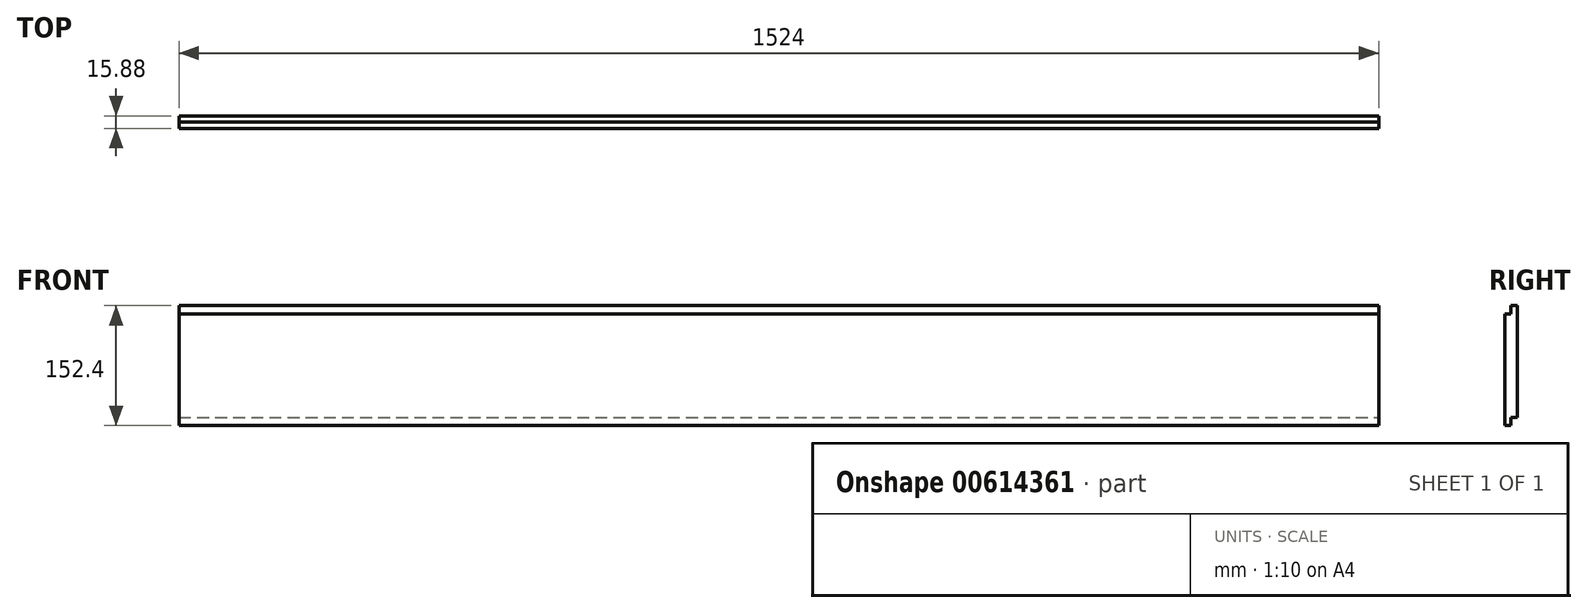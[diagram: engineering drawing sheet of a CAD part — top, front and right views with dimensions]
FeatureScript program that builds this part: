
annotation { "Feature Type Name" : "Feature", "Feature Type Description" : "" }
export const myFeature = defineFeature(function(context is Context, id is Id, definition is map)
    precondition{}
    {
        {
            var Q0;
            Q0=qCreatedBy(makeId("Front.planeOp"),FACE);
            var sketch = newSketch(context, id + "F0", { "sketchPlane" : qUnion([Q0])});
            skLineSegment(sketch, "E0", {"start": v(0, 0) * mm, "end": v(762, 0) * mm});
            skLineSegment(sketch, "E1", {"start": v(762, 0) * mm, "end": v(762, 76.2) * mm});
            skLineSegment(sketch, "E2.bottom", {"start": v(762, 76.2) * mm, "end": v(-762, 76.2) * mm});
            skLineSegment(sketch, "E2.top", {"start": v(762, -76.2) * mm, "end": v(-762, -76.2) * mm});
            skLineSegment(sketch, "E2.left", {"start": v(762, 76.2) * mm, "end": v(762, -76.2) * mm});
            skLineSegment(sketch, "E2.right", {"start": v(-762, 76.2) * mm, "end": v(-762, -76.2) * mm});
            skPoint(sketch, "E2.middle", {"position": v(0, 0) * mm});
            skSolve(sketch);
        }
        {
            var Q0;
            Q0=qSketchRegion(id+"F0",true);
            extrude(context, id + "F1", {"entities" : qUnion([Q0]), "depth" : 15.88 * mm, "offsetDistance" : 25.4 * mm});
        }
        {
            var Q0;
            Q0=makeQuery(id+"F1.opExtrude","SWEPT_FACE",FACE,{"disambiguationData":[OSD([sQuery(id+"F0.wireOp",EDGE,"E2.left")])]});
            var sketch = newSketch(context, id + "F2", { "sketchPlane" : qUnion([Q0])});
            skLineSegment(sketch, "E3", {"start": v(0, 76.2) * mm, "end": v(-7.87, 76.2) * mm});
            skLineSegment(sketch, "E4", {"start": v(-7.87, 76.2) * mm, "end": v(-7.87, 65.79) * mm});
            skLineSegment(sketch, "E5.bottom", {"start": v(-15.88, 76.2) * mm, "end": v(-7.87, 76.2) * mm});
            skLineSegment(sketch, "E5.top", {"start": v(-15.88, 65.79) * mm, "end": v(-7.87, 65.79) * mm});
            skLineSegment(sketch, "E5.left", {"start": v(-15.88, 76.2) * mm, "end": v(-15.88, 65.79) * mm});
            skLineSegment(sketch, "E6", {"start": v(-15.88, -76.2) * mm, "end": v(-8, -76.2) * mm});
            skLineSegment(sketch, "E7", {"start": v(-8, -76.2) * mm, "end": v(-8, -65.79) * mm});
            skLineSegment(sketch, "E8.bottom", {"start": v(0, -76.2) * mm, "end": v(-8, -76.2) * mm});
            skLineSegment(sketch, "E8.top", {"start": v(0, -65.79) * mm, "end": v(-8, -65.79) * mm});
            skLineSegment(sketch, "E8.left", {"start": v(0, -76.2) * mm, "end": v(0, -65.79) * mm});
            skSolve(sketch);
        }
        {
            var Q0;
            Q0=makeQuery(id+"F2.imprint","IMPRINT",FACE,{"disambiguationData":[TD([[makeQuery(id+"F2.imprint","IMPRINT",EDGE,{"derivedFrom":sQuery(id+"F2.wireOp",EDGE,"E8.bottom")}),1.0]])]});
            var Q1;
            Q1=makeQuery(id+"F2.imprint","IMPRINT",FACE,{"disambiguationData":[TD([[makeQuery(id+"F2.imprint","IMPRINT",EDGE,{"derivedFrom":sQuery(id+"F2.wireOp",EDGE,"E5.bottom")}),-1.0]])]});
            extrude(context, id + "F3", {"entities" : qUnion([Q0, Q1]), "operationType" : NewBodyOperationType.REMOVE, "endBound" : BoundingType.UP_TO_NEXT, "oppositeDirection" : true, "depth" : 25.4 * mm, "offsetDistance" : 25.4 * mm});
        }
    });
